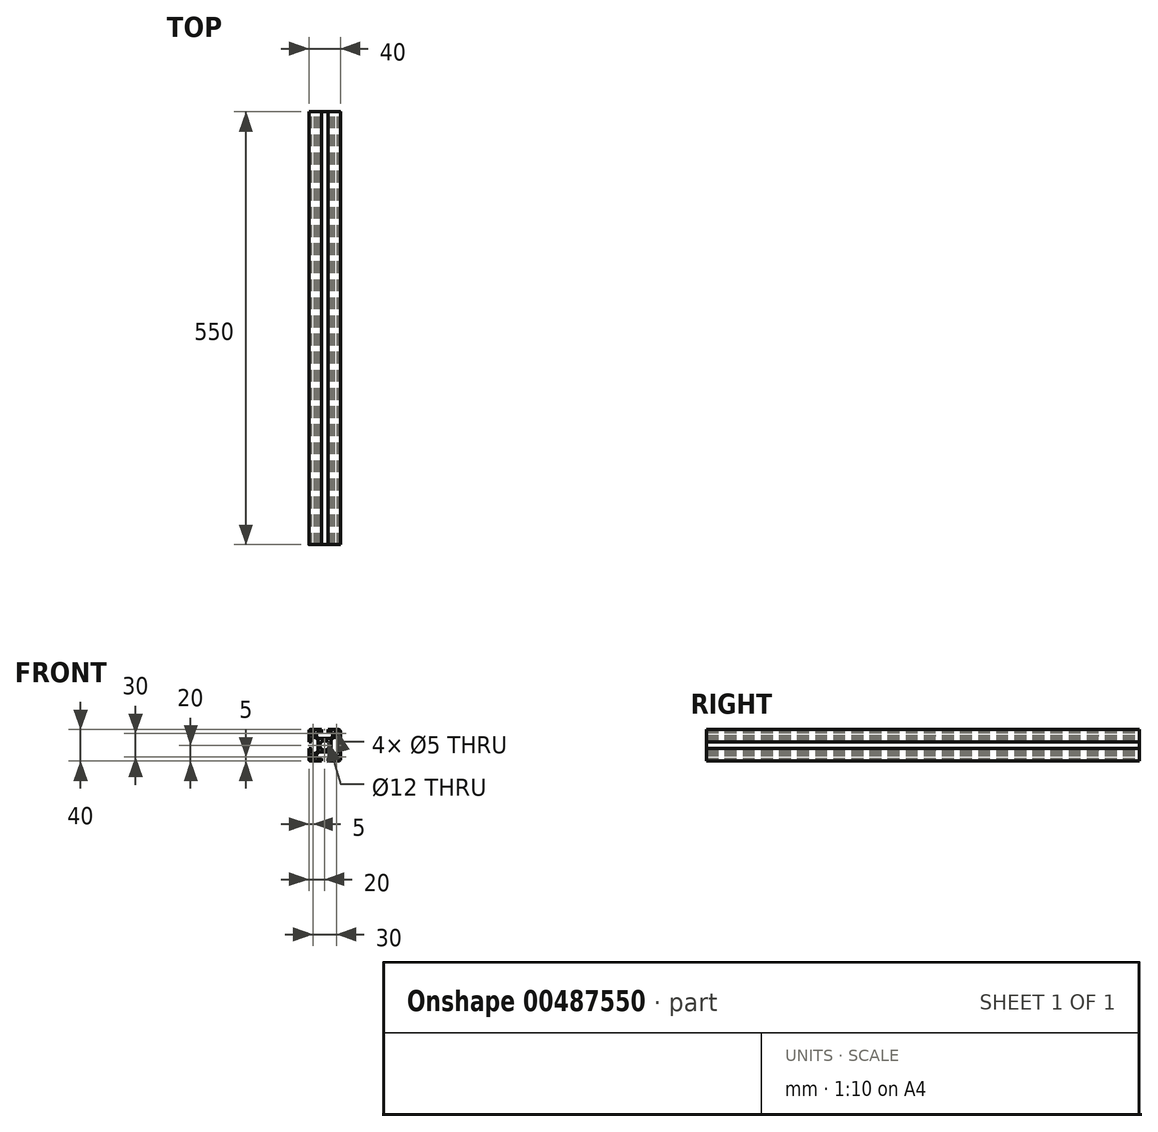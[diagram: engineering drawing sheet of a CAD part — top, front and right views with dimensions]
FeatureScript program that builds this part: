
annotation { "Feature Type Name" : "Feature", "Feature Type Description" : "" }
export const myFeature = defineFeature(function(context is Context, id is Id, definition is map)
    precondition{}
    {
        {
            var Q0;
            Q0=qCreatedBy(makeId("Front.planeOp"),FACE);
            var sketch = newSketch(context, id + "F0", { "sketchPlane" : qUnion([Q0])});
            skLineSegment(sketch, "E0.bottom", {"start": v(20, -20) * mm, "end": v(-20, -20) * mm});
            skLineSegment(sketch, "E0.top", {"start": v(20, 20) * mm, "end": v(-20, 20) * mm});
            skLineSegment(sketch, "E0.left", {"start": v(20, -20) * mm, "end": v(20, 20) * mm});
            skLineSegment(sketch, "E0.right", {"start": v(-20, -20) * mm, "end": v(-20, 20) * mm});
            skPoint(sketch, "E0.middle", {"position": v(0, 0) * mm});
            skCircle(sketch, "E1", {"center": v(0, 0) * mm, "radius": 6 * mm});
            skLineSegment(sketch, "E2", {"start": v(20, 15) * mm, "end": v(-20, 15) * mm, "construction": true});
            skLineSegment(sketch, "E3", {"start": v(20, -15) * mm, "end": v(-20, -15) * mm, "construction": true});
            skLineSegment(sketch, "E4", {"start": v(-15, -20) * mm, "end": v(-15, 20) * mm, "construction": true});
            skLineSegment(sketch, "E5", {"start": v(15, -20) * mm, "end": v(15, 20) * mm, "construction": true});
            skCircle(sketch, "E6", {"center": v(-15, 15) * mm, "radius": 2.5 * mm});
            skCircle(sketch, "E7", {"center": v(-15, -15) * mm, "radius": 2.5 * mm});
            skLineSegment(sketch, "E8", {"start": v(-4.1, 20) * mm, "end": v(-4.1, 16.5) * mm});
            skLineSegment(sketch, "E9", {"start": v(-4.1, 16.5) * mm, "end": v(-10, 16.5) * mm});
            skLineSegment(sketch, "E10", {"start": v(-10, 16.5) * mm, "end": v(-10, 11.4) * mm});
            skLineSegment(sketch, "E11", {"start": v(-10, 11.4) * mm, "end": v(-7.1, 8.5) * mm});
            skLineSegment(sketch, "E12", {"start": v(-7.1, 8.5) * mm, "end": v(0, 8.5) * mm});
            skLineSegment(sketch, "E13", {"start": v(0, 8.5) * mm, "end": v(0, 20) * mm});
            skLineSegment(sketch, "E14.MirrorCS", {"start": v(7.1, 8.5) * mm, "end": v(0, 8.5) * mm});
            skLineSegment(sketch, "E15.MirrorCS", {"start": v(10, 11.4) * mm, "end": v(7.1, 8.5) * mm});
            skLineSegment(sketch, "E16.MirrorCS", {"start": v(10, 16.5) * mm, "end": v(10, 11.4) * mm});
            skLineSegment(sketch, "E17.MirrorCS", {"start": v(4.1, 16.5) * mm, "end": v(10, 16.5) * mm});
            skLineSegment(sketch, "E18.MirrorCS", {"start": v(4.1, 20) * mm, "end": v(4.1, 16.5) * mm});
            skLineSegment(sketch, "E19.MirrorCS", {"start": v(7.1, -8.5) * mm, "end": v(0, -8.5) * mm});
            skLineSegment(sketch, "E20.MirrorCS", {"start": v(10, -11.4) * mm, "end": v(7.1, -8.5) * mm});
            skLineSegment(sketch, "E21.MirrorCS", {"start": v(10, -16.5) * mm, "end": v(10, -11.4) * mm});
            skLineSegment(sketch, "E22.MirrorCS", {"start": v(4.1, -16.5) * mm, "end": v(10, -16.5) * mm});
            skLineSegment(sketch, "E23.MirrorCS", {"start": v(4.1, -20) * mm, "end": v(4.1, -16.5) * mm});
            skLineSegment(sketch, "E24.MirrorCS", {"start": v(-4.1, -20) * mm, "end": v(-4.1, -16.5) * mm});
            skLineSegment(sketch, "E25.MirrorCS", {"start": v(-4.1, -16.5) * mm, "end": v(-10, -16.5) * mm});
            skLineSegment(sketch, "E26.MirrorCS", {"start": v(-10, -16.5) * mm, "end": v(-10, -11.4) * mm});
            skLineSegment(sketch, "E27.MirrorCS", {"start": v(-10, -11.4) * mm, "end": v(-7.1, -8.5) * mm});
            skLineSegment(sketch, "E28.MirrorCS", {"start": v(-7.1, -8.5) * mm, "end": v(0, -8.5) * mm});
            skCircle(sketch, "E29.MirrorC", {"center": v(15, -15) * mm, "radius": 2.5 * mm});
            skCircle(sketch, "E30.MirrorC", {"center": v(15, 15) * mm, "radius": 2.5 * mm});
            skLineSegment(sketch, "E31", {"start": v(-20, -4.1) * mm, "end": v(-16.5, -4.1) * mm});
            skLineSegment(sketch, "E32", {"start": v(-16.5, -4.1) * mm, "end": v(-16.5, -10) * mm});
            skLineSegment(sketch, "E33", {"start": v(-16.5, -10) * mm, "end": v(-11.4, -10) * mm});
            skLineSegment(sketch, "E34", {"start": v(-11.4, -10) * mm, "end": v(-8.5, -7.1) * mm});
            skLineSegment(sketch, "E35", {"start": v(-8.5, -7.1) * mm, "end": v(-8.5, 0) * mm});
            skLineSegment(sketch, "E36", {"start": v(-8.5, 0) * mm, "end": v(-20, 0) * mm});
            skLineSegment(sketch, "E37.MirrorCS", {"start": v(-8.5, 7.1) * mm, "end": v(-8.5, 0) * mm});
            skLineSegment(sketch, "E38.MirrorCS", {"start": v(-11.4, 10) * mm, "end": v(-8.5, 7.1) * mm});
            skLineSegment(sketch, "E39.MirrorCS", {"start": v(-16.5, 10) * mm, "end": v(-11.4, 10) * mm});
            skLineSegment(sketch, "E40.MirrorCS", {"start": v(-16.5, 4.1) * mm, "end": v(-16.5, 10) * mm});
            skLineSegment(sketch, "E41.MirrorCS", {"start": v(-20, 4.1) * mm, "end": v(-16.5, 4.1) * mm});
            skLineSegment(sketch, "E42.MirrorCS", {"start": v(8.5, 7.1) * mm, "end": v(8.5, 0) * mm});
            skLineSegment(sketch, "E43.MirrorCS", {"start": v(8.5, -7.1) * mm, "end": v(8.5, 0) * mm});
            skLineSegment(sketch, "E44.MirrorCS", {"start": v(11.4, -10) * mm, "end": v(8.5, -7.1) * mm});
            skLineSegment(sketch, "E45.MirrorCS", {"start": v(11.4, 10) * mm, "end": v(8.5, 7.1) * mm});
            skLineSegment(sketch, "E46.MirrorCS", {"start": v(16.5, 10) * mm, "end": v(11.4, 10) * mm});
            skLineSegment(sketch, "E47.MirrorCS", {"start": v(16.5, -10) * mm, "end": v(11.4, -10) * mm});
            skLineSegment(sketch, "E48.MirrorCS", {"start": v(16.5, -4.1) * mm, "end": v(16.5, -10) * mm});
            skLineSegment(sketch, "E49.MirrorCS", {"start": v(16.5, 4.1) * mm, "end": v(16.5, 10) * mm});
            skLineSegment(sketch, "E50.MirrorCS", {"start": v(20, 4.1) * mm, "end": v(16.5, 4.1) * mm});
            skLineSegment(sketch, "E51.MirrorCS", {"start": v(20, -4.1) * mm, "end": v(16.5, -4.1) * mm});
            skSolve(sketch);
        }
        {
            var Q0;
            Q0=makeQuery(id+"F0.imprint","IMPRINT",FACE,{"disambiguationData":[TD([[makeQuery(id+"F0.imprint","IMPRINT",EDGE,{"derivedFrom":sQuery(id+"F0.wireOp",EDGE,"E1")}),-1.0]])]});
            extrude(context, id + "F1", {"entities" : qUnion([Q0]), "depth" : 550 * mm, "offsetDistance" : 25 * mm});
        }
        {
            var Q0;
            Q0=makeQuery(id+"F1.opExtrude","SWEPT_EDGE",EDGE,{"disambiguationData":[OSD([sQuery(id+"F0.wireOp",EDGE,"E0.top"),sQuery(id+"F0.wireOp",EDGE,"E0.left")])]});
            var Q1;
            Q1=makeQuery(id+"F1.opExtrude","SWEPT_EDGE",EDGE,{"disambiguationData":[OSD([sQuery(id+"F0.wireOp",EDGE,"E0.top"),sQuery(id+"F0.wireOp",EDGE,"E0.right")])]});
            var Q2;
            Q2=makeQuery(id+"F1.opExtrude","SWEPT_EDGE",EDGE,{"disambiguationData":[OSD([sQuery(id+"F0.wireOp",EDGE,"E0.bottom"),sQuery(id+"F0.wireOp",EDGE,"E0.right")])]});
            var Q3;
            Q3=makeQuery(id+"F1.opExtrude","SWEPT_EDGE",EDGE,{"disambiguationData":[OSD([sQuery(id+"F0.wireOp",EDGE,"E0.bottom"),sQuery(id+"F0.wireOp",EDGE,"E0.left")])]});
            fillet(context, id + "F2", {"entities" : qUnion([Q0, Q1, Q2, Q3]), "radius" : 2 * mm, "tangentPropagation" : true, "allowEdgeOverflow" : false});
        }
    });
